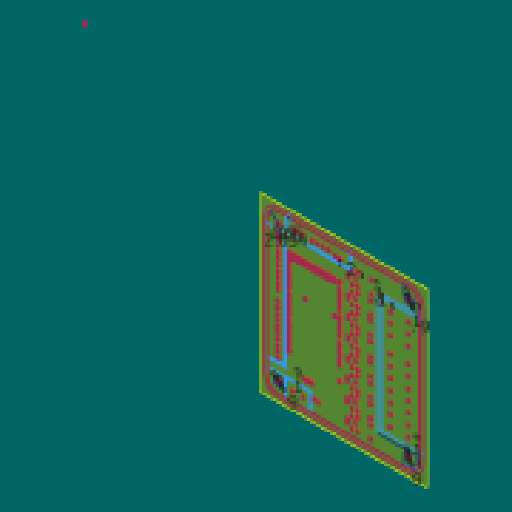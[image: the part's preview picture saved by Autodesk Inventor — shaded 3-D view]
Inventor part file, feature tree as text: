
AUTODESK INVENTOR PART (.ipt)
format: ipt  version: 2025.2 (Build 292293000, 293)  size: 385,024 bytes
history: native  units: mm
features: reference x8, other x3, extrude x2, fillet x2, sketch x2, plane x1
ambient origin geometry x8: Origin, YZ Plane, XZ Plane, XY Plane, X Axis, Y Axis, Z Axis, Center Point
bodies: Solid1 (feature_tree)
feature tree (18):
  plane  "Work Plane1"
  extrude  "Extrusion1"  Depth=9.0mm
  extrude  "Extrusion2"  Depth=1.0mm
  fillet  "Fillet1"  Radius=1.0mm
  fillet  "Fillet2"  Radius=3.0mm
  sketch  "Sketch1"  dims[d1=9.0mm d2=9.0mm]
  reference  "Reference1"
  reference  "Reference2"
  reference  "Reference3"
  reference  "Reference4"
  sketch  "Sketch2"  dims[d8=1.0mm d9=1.0mm d10=1.0mm d11=3.0mm d13=3.0mm d21=0.5mm d23=0.5mm d25=2.0mm d26=2.05429mm d27=21.085mm d28=0.0mm d33=2.0mm d34=10.0mm d35=0.0mm d36=2.0mm d37=3.0mm]
  reference  "Reference5"
  reference  "Reference6"
  reference  "Reference7"
  reference  "Reference8"
  other  "Assembly9"
  other  "BAS_Hardware:1"
  other  "Part_atas:1"
